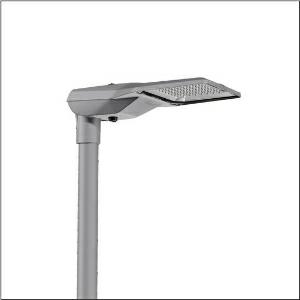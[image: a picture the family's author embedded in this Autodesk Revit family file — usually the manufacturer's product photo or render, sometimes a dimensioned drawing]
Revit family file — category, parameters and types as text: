
# Revit family: streetlight_sl_21_midi___st1_0ab_5xe3m32y08nb_2421
name_source: partatom
category: Lighting Fixtures
units: mm (PartAtom-declared; Revit-internal decimal feet)

## family parameters
Cut with Voids When Loaded = No
Host = Face
Light Source = No
Part Type = Normal
Room Calculation Point = No
Round Connector Dimension = Use Diameter
Shared = No

## types (1)
- --- (1 x LED, 19980 lm, 151.2 W, 3000K)
    Apparent Load = 151 VA
    CIE Flux Codes = 40 74 97 100 100
    Color Rendering = 70
    Color Temperature = 3000K
    Default Elevation = 1800 mm
    Description = Streetlight SL 21 midi, mast luminaire, primary light control with lens, of PMMA, primary optical cover: cover, of toughened safety glass, transparent, light distribution: ST1.0aB, light emission: direct distribution, primary light characteristic: asymmetric, installation type: side-entry, post-top, LED, High Power LED, rated luminous flux: 19.980lm, luminous efficacy: 132lm/W, light colour: 730, colour temperature: 3000K, control gear: D4i with power reduction, control: flexible luminous flux parameterisation, time-dependent luminous flux control, constant luminous flux control, overheat protection, power reduction, pre-setting: logarithmic dimming characteristic, mains connection: 230..240V, AC, 50/60Hz, start of lifetime: 151W, end of service life: 157W, reduction: 70W, luminaire housing, of diecast aluminium, powder-coated, SITECO metallic grey (DB 702S), corrosivity category C5 high according to DIN EN ISO 12944, please order mast flange separately, inclination adjustable: 0°, 5°, 10°, 15°, sealing non-destructively replaceable, multi-level sealing system, length: 644mm, width: 335mm, height: 110mm, mast flange for spigot size: 42mm (side-entry): 5XC10008XM4, 60/48mm (side-entry/post-top): 5XC10108XM2, 76/60mm (side-entry/post-top): 5XC10108XM1, mounting height: 4..8m, Smart Interface below and above, protection rating (complete): IP66, insulation class (complete): insulation class II (safety insulation), certification: CE, ENEC, ENEC+, VDE, impact resistance: IK10, permissible operating ambient temperature for outdoor applications: -40..+50°C, standard-compliant lighting for roads and squares, packaging unit: 1 piece

Light Distribution: ST1.0aB
    Height = 111 mm
    Lamp = 1 x LED
    Lamp Light Flux = 19980 lm
    Lamp Power = 151.2 W
    Lamp count = 1
    Length = 644 mm
    Luminous efficacy = 132 lm/W
    Manufacturer = Siteco
    ModVariant = No
    Model = 5XE3M32Y08NB
    Number of Poles = 1
    OnlyDefault = Yes
    Power Factor = 1
    Product Name = Streetlight SL 21 midi | ST1.0aB
    Product group = mast luminaire | pylon top
    ProductGroupID = 6100
    Protection Class = Protection class II
    Protection Degree = IP 66
    RLX_Detail_Level = 1
    RLX_Emergency_Light_Flux = 0 lm
    RLX_Emergency_Type = 0
    RLX_Emergency_Type_DB = No
    RlxData = <blob elided: 27133 chars, md5=5f5301c8>
    Socket = socket
    Standby Power = 0 W
    System Light Flux = 19980 lm
    System Power = 151 W
    Type Comments = factory setting: luminous flux: 100 % | dim-lin: 254 | 802 mA
    Type Image = l_1004304.jpg
    URL = http://relux.com
    VarID = @adj_167547
    Voltage = 0 V
    Weight = 0.00 kg
    Width = 336 mm

## geometry (parser evidence)
native form markers: Blend x4, Sweep x14
no freeform markers — native parametric forms only
